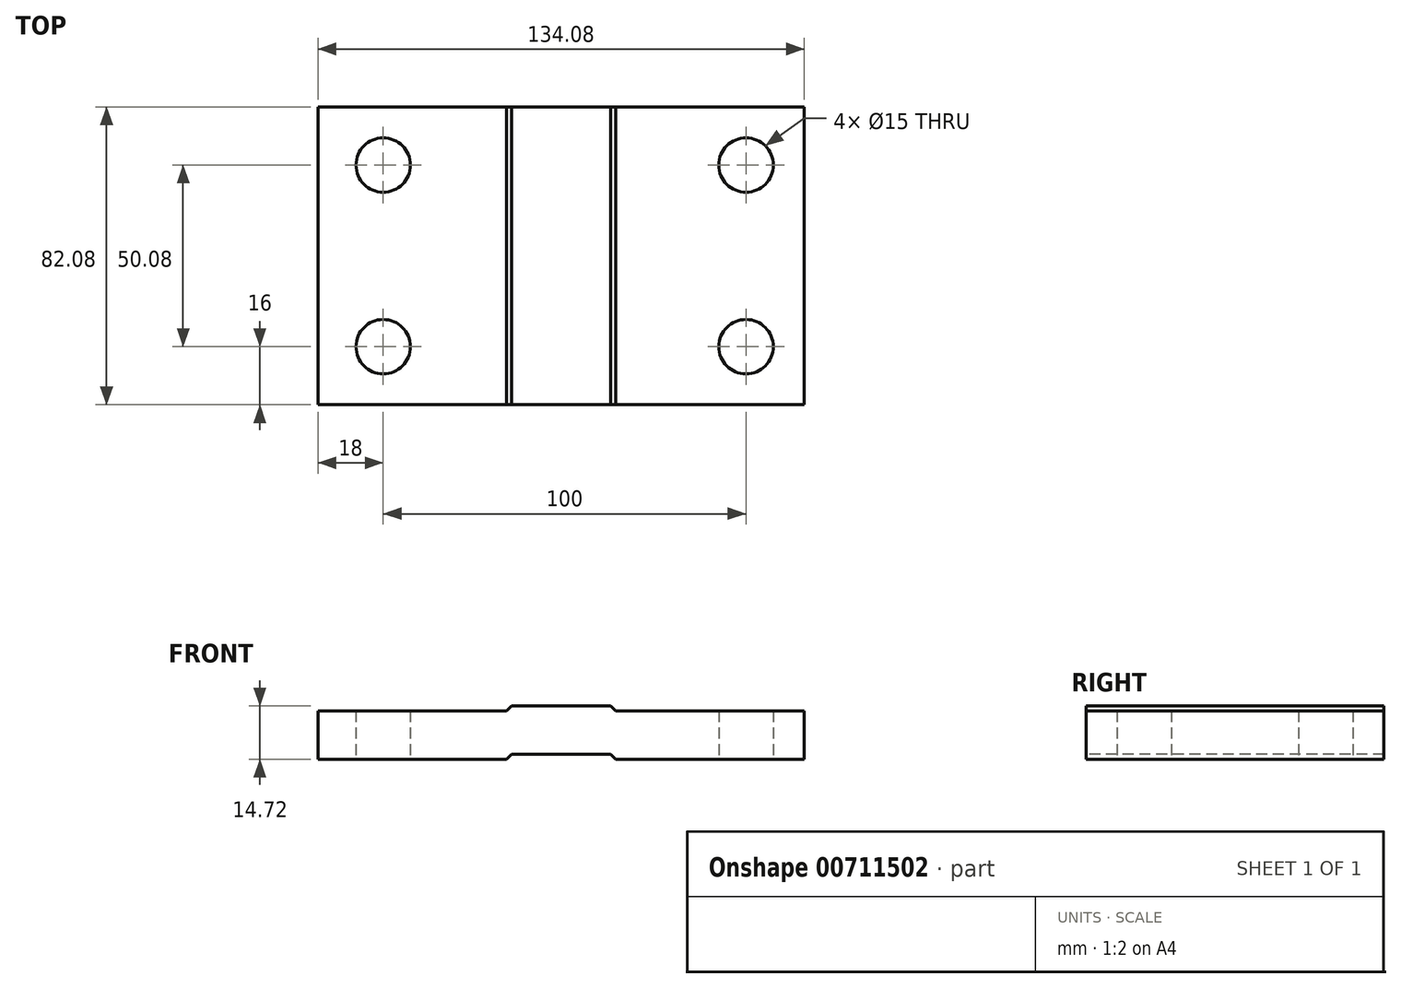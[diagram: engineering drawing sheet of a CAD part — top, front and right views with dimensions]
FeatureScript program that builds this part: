
annotation { "Feature Type Name" : "Feature", "Feature Type Description" : "" }
export const myFeature = defineFeature(function(context is Context, id is Id, definition is map)
    precondition{}
    {
        {
            var Q0;
            Q0=qCreatedBy(makeId("Top.planeOp"),FACE);
            var sketch = newSketch(context, id + "F0", { "sketchPlane" : qUnion([Q0])});
            skLineSegment(sketch, "E0", {"start": v(0, 0) * mm, "end": v(-67.04, 0) * mm});
            skLineSegment(sketch, "E1.MirrorCS", {"start": v(0, 0) * mm, "end": v(67.04, 0) * mm});
            skLineSegment(sketch, "E2", {"start": v(-67.04, 0) * mm, "end": v(-67.04, 82.08) * mm});
            skLineSegment(sketch, "E3", {"start": v(-67.04, 82.08) * mm, "end": v(67.04, 82.08) * mm});
            skLineSegment(sketch, "E4", {"start": v(67.04, 82.08) * mm, "end": v(67.04, 0) * mm});
            skSolve(sketch);
        }
        {
            var Q0;
            Q0=makeQuery(id+"F0.imprint","IMPRINT",FACE,{"disambiguationData":[TD([[makeQuery(id+"F0.imprint","IMPRINT",EDGE,{"derivedFrom":sQuery(id+"F0.wireOp",EDGE,"E0")}),-1.0]])]});
            extrude(context, id + "F1", {"entities" : qUnion([Q0]), "depth" : 13.32 * mm, "offsetDistance" : 25 * mm});
        }
        {
            var Q0;
            Q0=makeQuery(id+"F1.opExtrude","SWEPT_FACE",FACE,{"disambiguationData":[OSD([sQuery(id+"F0.wireOp",EDGE,"E0"),sQuery(id+"F0.wireOp",EDGE,"E1.MirrorCS")])]});
            cPlane(context, id + "F2", {"entities" : qUnion([Q0]), "cplaneType" : CPlaneType.OFFSET, "offset" : 0 * mm, "width" : 150 * mm, "height" : 150 * mm});
        }
        {
            var Q0;
            Q0=qCreatedBy(id+"F2.planeOp",FACE);
            var sketch = newSketch(context, id + "F3", { "sketchPlane" : qUnion([Q0])});
            skLineSegment(sketch, "E5", {"start": v(0, 0) * mm, "end": v(-15, 0) * mm});
            skLineSegment(sketch, "E6.MirrorCS", {"start": v(0, 0) * mm, "end": v(15, 0) * mm});
            skLineSegment(sketch, "E7", {"start": v(-13.6, 1.4) * mm, "end": v(13.6, 1.4) * mm});
            skLineSegment(sketch, "E8", {"start": v(-15, 0) * mm, "end": v(-13.6, 1.4) * mm});
            skLineSegment(sketch, "E9", {"start": v(15, 0) * mm, "end": v(13.6, 1.4) * mm});
            skSolve(sketch);
        }
        {
            var Q0;
            Q0=makeQuery(id+"F3.imprint","IMPRINT",FACE,{"disambiguationData":[TD([[makeQuery(id+"F3.imprint","IMPRINT",EDGE,{"derivedFrom":sQuery(id+"F3.wireOp",EDGE,"E5")}),-1.0]])]});
            extrude(context, id + "F4", {"entities" : qUnion([Q0]), "operationType" : NewBodyOperationType.REMOVE, "endBound" : BoundingType.THROUGH_ALL, "oppositeDirection" : true, "depth" : 25 * mm, "offsetDistance" : 25 * mm});
        }
        {
            var Q0;
            Q0=qCreatedBy(id+"F2.planeOp",FACE);
            cPlane(context, id + "F5", {"entities" : qUnion([Q0]), "cplaneType" : CPlaneType.OFFSET, "offset" : 0 * mm, "width" : 150 * mm, "height" : 150 * mm});
        }
        {
            var Q0;
            Q0=qCreatedBy(id+"F5.planeOp",FACE);
            var sketch = newSketch(context, id + "F6", { "sketchPlane" : qUnion([Q0])});
            skPoint(sketch, "E10", {"position": v(0, 13.32) * mm});
            skLineSegment(sketch, "E11", {"start": v(0, 13.32) * mm, "end": v(-15, 13.32) * mm});
            skLineSegment(sketch, "E12.MirrorCS", {"start": v(0, 13.32) * mm, "end": v(15, 13.32) * mm});
            skLineSegment(sketch, "E13", {"start": v(-13.6, 14.72) * mm, "end": v(13.6, 14.72) * mm});
            skLineSegment(sketch, "E14", {"start": v(-15, 13.32) * mm, "end": v(-13.6, 14.72) * mm});
            skLineSegment(sketch, "E15", {"start": v(15, 13.32) * mm, "end": v(13.6, 14.72) * mm});
            skSolve(sketch);
        }
        {
            var Q0;
            Q0=makeQuery(id+"F6.imprint","IMPRINT",FACE,{"disambiguationData":[TD([[makeQuery(id+"F6.imprint","IMPRINT",EDGE,{"derivedFrom":sQuery(id+"F6.wireOp",EDGE,"E11")}),-1.0]])]});
            extrude(context, id + "F7", {"entities" : qUnion([Q0]), "operationType" : NewBodyOperationType.ADD, "oppositeDirection" : true, "depth" : 82.08 * mm, "offsetDistance" : 25 * mm});
        }
        {
            var Q0;
            Q0=qCreatedBy(makeId("Top.planeOp"),FACE);
            var sketch = newSketch(context, id + "F8", { "sketchPlane" : qUnion([Q0])});
            skPoint(sketch, "E16", {"position": v(-49.04, 16) * mm});
            skPoint(sketch, "E17", {"position": v(50.96, 16) * mm});
            skPoint(sketch, "E18", {"position": v(50.96, 66.08) * mm});
            skPoint(sketch, "E19", {"position": v(-49.04, 66.08) * mm});
            skSolve(sketch);
        }
        {
            var Q0;
            Q0=sQuery(id+"F8.wireOp",VERTEX,"E19");
            var Q1;
            Q1=sQuery(id+"F8.wireOp",VERTEX,"E16");
            var Q2;
            Q2=sQuery(id+"F8.wireOp",VERTEX,"E17");
            var Q3;
            Q3=sQuery(id+"F8.wireOp",VERTEX,"E18");
            var Q4;
            Q4=makeQuery(id+"F1.opExtrude","SWEPT_BODY",BODY,{"disambiguationData":[OSD([sQuery(id+"F0.wireOp",EDGE,"E0"),sQuery(id+"F0.wireOp",EDGE,"E1.MirrorCS"),sQuery(id+"F0.wireOp",EDGE,"E2"),sQuery(id+"F0.wireOp",EDGE,"E3"),sQuery(id+"F0.wireOp",EDGE,"E4")])]});
            hole(context, id + "F9", {"style" : HoleStyle.SIMPLE, "endStyle" : HoleEndStyle.THROUGH, "oppositeDirection" : true, "holeDiameter" : 15 * mm, "majorDiameter" : 5 * mm, "isTappedThrough" : true, "tappedDepth" : 12 * mm, "tapClearance" : 3, "locations" : qUnion([Q0, Q1, Q2, Q3]), "scope" : qUnion([Q4])});
        }
    });
